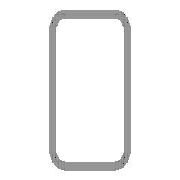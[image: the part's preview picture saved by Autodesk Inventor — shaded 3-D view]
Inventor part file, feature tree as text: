
AUTODESK INVENTOR PART (.ipt)
format: ipt  version: 2025 (Build 290162010, 162A)  size: 132,608 bytes
history: native  units: mm (DEFAULTED — no unit token found)
features: other x4, sketch x1, plane x1
ambient origin geometry x8: Origin, YZ Plane, XZ Plane, XY Plane, X Axis, Y Axis, Z Axis, Center Point
bodies: Solid1 (feature_tree), Body (feature_tree)
feature tree (6):
  parser-record x1  (decoder bookkeeping rows leaked as tree rows — omitted from the tree; the rows remain in map.json)
  other  "Driven Length"
  other  "Start Plane"
  other  "End Plane"
  sketch  "Sketch3"  dims[d3=770.0mm d4=0.0mm d7=6.0mm d9=40.0mm d11=80.0mm d12=3.0mm d13=-0.0mm d14=770.0mm d15=20.0mm d16=40.0mm d17=90.0deg d18=770.0mm]
  plane  "Work Plane3"
